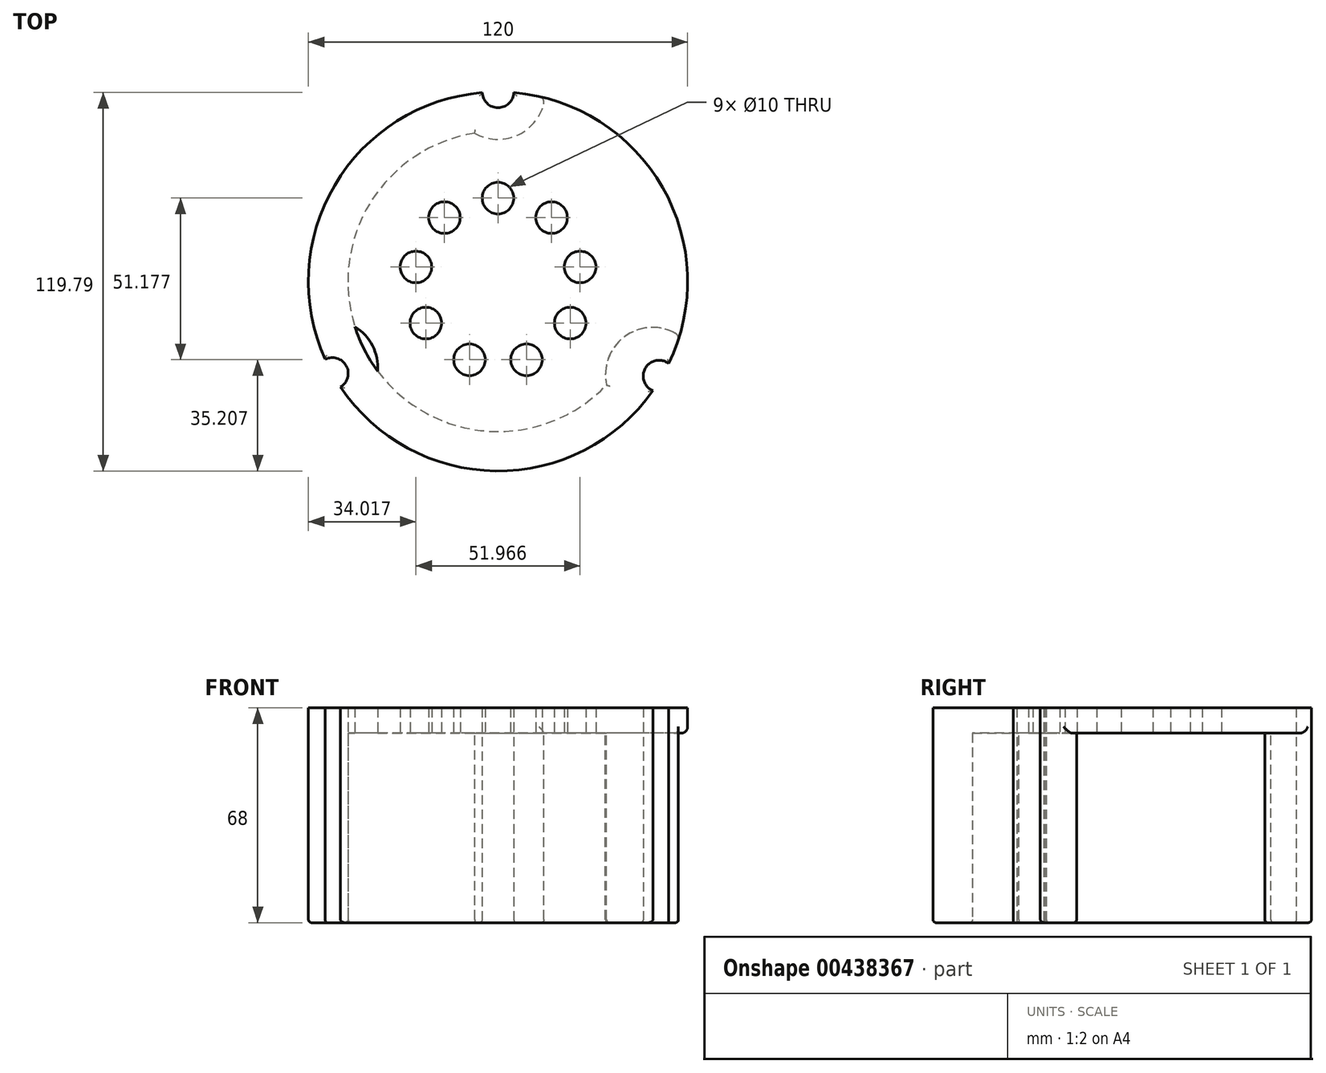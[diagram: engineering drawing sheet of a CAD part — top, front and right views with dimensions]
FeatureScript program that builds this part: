
annotation { "Feature Type Name" : "Feature", "Feature Type Description" : "" }
export const myFeature = defineFeature(function(context is Context, id is Id, definition is map)
    precondition{}
    {
        {
            var Q0;
            Q0=qCreatedBy(makeId("Top.planeOp"),FACE);
            var sketch = newSketch(context, id + "F0", { "sketchPlane" : qUnion([Q0])});
            skCircle(sketch, "E0", {"center": v(0, 0) * mm, "radius": 60 * mm});
            skArc(sketch, "E1", {"start": v(-14.88, 58.12) * mm, "mid": v(0, 45) * mm, "end": v(14.88, 58.12) * mm});
            skArc(sketch, "E2.1.0", {"start": v(-44.9, -39.8) * mm, "mid": v(-39.7, -20.36) * mm, "end": v(-58.52, -13.24) * mm});
            skArc(sketch, "E2.2.0", {"start": v(57.49, -17.18) * mm, "mid": v(36.15, -21.8) * mm, "end": v(42.02, -42.83) * mm});
            skPoint(sketch, "E2.center", {"position": v(-1.35, 1.08) * mm});
            skCircle(sketch, "E3", {"center": v(0, 0) * mm, "radius": 47.5 * mm});
            skArc(sketch, "E4", {"start": v(-5, 59.8) * mm, "mid": v(0, 55) * mm, "end": v(5, 59.8) * mm});
            skArc(sketch, "E5.1.0", {"start": v(-49.85, -33.4) * mm, "mid": v(-48.05, -26.68) * mm, "end": v(-54.7, -24.66) * mm});
            skArc(sketch, "E5.2.0", {"start": v(54.06, -26.03) * mm, "mid": v(46.65, -27.42) * mm, "end": v(49.04, -34.57) * mm});
            skPoint(sketch, "E5.center", {"position": v(-0.48, 0.31) * mm});
            skCircle(sketch, "E6", {"center": v(0, 26.38) * mm, "radius": 5 * mm});
            skCircle(sketch, "E7.1.0", {"center": v(-16.96, 20.21) * mm, "radius": 5 * mm});
            skCircle(sketch, "E7.2.0", {"center": v(-25.98, 4.58) * mm, "radius": 5 * mm});
            skCircle(sketch, "E7.3.0", {"center": v(-22.85, -13.2) * mm, "radius": 5 * mm});
            skCircle(sketch, "E7.4.0", {"center": v(-9.02, -24.8) * mm, "radius": 5 * mm});
            skCircle(sketch, "E7.5.0", {"center": v(9.02, -24.8) * mm, "radius": 5 * mm});
            skCircle(sketch, "E7.6.0", {"center": v(22.85, -13.2) * mm, "radius": 5 * mm});
            skCircle(sketch, "E7.7.0", {"center": v(25.98, 4.58) * mm, "radius": 5 * mm});
            skCircle(sketch, "E7.8.0", {"center": v(16.96, 20.21) * mm, "radius": 5 * mm});
            skSolve(sketch);
        }
        {
            var Q0;
            {var subQ0=sQuery(id+"F0.wireOp",EDGE,"E3");var subQ1=sQuery(id+"F0.wireOp",EDGE,"E1");var subQ2=makeQuery(id+"F0.imprint","INTERSECT",VERTEX,{"disambiguationData":[OD(0.0)],"derivedFrom":[subQ1,subQ0]});Q0=makeQuery(id+"F0.imprint","IMPRINT",FACE,{"disambiguationData":[TD([[makeQuery(id+"F0.imprint","IMPRINT",EDGE,{"disambiguationData":[TD([[subQ2,-1.0]])],"derivedFrom":subQ1}),-1.0]])]});}
            var Q1;
            {var subQ0=sQuery(id+"F0.wireOp",EDGE,"E3");var subQ1=sQuery(id+"F0.wireOp",EDGE,"E2.1.0");var subQ2=makeQuery(id+"F0.imprint","INTERSECT",VERTEX,{"disambiguationData":[OD(0.0)],"derivedFrom":[subQ1,subQ0]});Q1=makeQuery(id+"F0.imprint","IMPRINT",FACE,{"disambiguationData":[TD([[makeQuery(id+"F0.imprint","IMPRINT",EDGE,{"disambiguationData":[TD([[subQ2,-1.0]])],"derivedFrom":subQ1}),1.0]])]});}
            var Q2;
            {var subQ0=sQuery(id+"F0.wireOp",EDGE,"E2.1.0");var subQ1=sQuery(id+"F0.wireOp",EDGE,"E0");var subQ2=makeQuery(id+"F0.imprint","INTERSECT",VERTEX,{"disambiguationData":[OD(0.0)],"derivedFrom":[subQ1,subQ0]});Q2=makeQuery(id+"F0.imprint","IMPRINT",FACE,{"disambiguationData":[TD([[makeQuery(id+"F0.imprint","IMPRINT",EDGE,{"disambiguationData":[TD([[subQ2,1.0]])],"derivedFrom":subQ1}),1.0]])]});}
            var Q3;
            {var subQ0=sQuery(id+"F0.wireOp",EDGE,"E2.1.0");var subQ1=sQuery(id+"F0.wireOp",EDGE,"E0");var subQ2=makeQuery(id+"F0.imprint","INTERSECT",VERTEX,{"disambiguationData":[OD(0.0)],"derivedFrom":[subQ1,subQ0]});Q3=makeQuery(id+"F0.imprint","IMPRINT",FACE,{"disambiguationData":[TD([[makeQuery(id+"F0.imprint","IMPRINT",EDGE,{"disambiguationData":[TD([[subQ2,-1.0]])],"derivedFrom":subQ1}),1.0]])]});}
            var Q4;
            {var subQ0=sQuery(id+"F0.wireOp",EDGE,"E2.2.0");var subQ1=sQuery(id+"F0.wireOp",EDGE,"E0");var subQ2=makeQuery(id+"F0.imprint","INTERSECT",VERTEX,{"disambiguationData":[OD(0.0)],"derivedFrom":[subQ1,subQ0]});Q4=makeQuery(id+"F0.imprint","IMPRINT",FACE,{"disambiguationData":[TD([[makeQuery(id+"F0.imprint","IMPRINT",EDGE,{"disambiguationData":[TD([[subQ2,1.0]])],"derivedFrom":subQ1}),1.0]])]});}
            var Q5;
            {var subQ0=sQuery(id+"F0.wireOp",EDGE,"E3");var subQ1=sQuery(id+"F0.wireOp",EDGE,"E2.2.0");var subQ2=makeQuery(id+"F0.imprint","INTERSECT",VERTEX,{"disambiguationData":[OD(0.0)],"derivedFrom":[subQ1,subQ0]});Q5=makeQuery(id+"F0.imprint","IMPRINT",FACE,{"disambiguationData":[TD([[makeQuery(id+"F0.imprint","IMPRINT",EDGE,{"disambiguationData":[TD([[subQ2,-1.0]])],"derivedFrom":subQ1}),1.0]])]});}
            var Q6;
            {var subQ0=sQuery(id+"F0.wireOp",EDGE,"E1");var subQ1=sQuery(id+"F0.wireOp",EDGE,"E0");var subQ2=makeQuery(id+"F0.imprint","INTERSECT",VERTEX,{"disambiguationData":[OD(1.0)],"derivedFrom":[subQ1,subQ0]});Q6=makeQuery(id+"F0.imprint","IMPRINT",FACE,{"disambiguationData":[TD([[makeQuery(id+"F0.imprint","IMPRINT",EDGE,{"disambiguationData":[TD([[subQ2,1.0]])],"derivedFrom":subQ1}),1.0]])]});}
            var Q7;
            {var subQ0=sQuery(id+"F0.wireOp",EDGE,"E1");var subQ1=sQuery(id+"F0.wireOp",EDGE,"E0");var subQ2=makeQuery(id+"F0.imprint","INTERSECT",VERTEX,{"disambiguationData":[OD(0.0)],"derivedFrom":[subQ1,subQ0]});Q7=makeQuery(id+"F0.imprint","IMPRINT",FACE,{"disambiguationData":[TD([[makeQuery(id+"F0.imprint","IMPRINT",EDGE,{"disambiguationData":[TD([[subQ2,1.0]])],"derivedFrom":subQ1}),1.0]])]});}
            var Q8;
            {var subQ0=sQuery(id+"F0.wireOp",EDGE,"E3");var subQ1=sQuery(id+"F0.wireOp",EDGE,"E1");var subQ2=makeQuery(id+"F0.imprint","INTERSECT",VERTEX,{"disambiguationData":[OD(0.0)],"derivedFrom":[subQ1,subQ0]});Q8=makeQuery(id+"F0.imprint","IMPRINT",FACE,{"disambiguationData":[TD([[makeQuery(id+"F0.imprint","IMPRINT",EDGE,{"disambiguationData":[TD([[subQ2,-1.0]])],"derivedFrom":subQ1}),1.0]])]});}
            var Q9;
            {var subQ0=sQuery(id+"F0.wireOp",EDGE,"E1");var subQ1=sQuery(id+"F0.wireOp",EDGE,"E0");var subQ2=makeQuery(id+"F0.imprint","INTERSECT",VERTEX,{"disambiguationData":[OD(0.0)],"derivedFrom":[subQ1,subQ0]});Q9=makeQuery(id+"F0.imprint","IMPRINT",FACE,{"disambiguationData":[TD([[makeQuery(id+"F0.imprint","IMPRINT",EDGE,{"disambiguationData":[TD([[subQ2,-1.0]])],"derivedFrom":subQ1}),1.0]])]});}
            var Q10;
            {var subQ0=sQuery(id+"F0.wireOp",EDGE,"E1");var subQ1=sQuery(id+"F0.wireOp",EDGE,"E0");var subQ2=makeQuery(id+"F0.imprint","INTERSECT",VERTEX,{"disambiguationData":[OD(1.0)],"derivedFrom":[subQ1,subQ0]});Q10=makeQuery(id+"F0.imprint","IMPRINT",FACE,{"disambiguationData":[TD([[makeQuery(id+"F0.imprint","IMPRINT",EDGE,{"disambiguationData":[TD([[subQ2,-1.0]])],"derivedFrom":subQ1}),1.0]])]});}
            var Q11;
            {var subQ0=sQuery(id+"F0.wireOp",EDGE,"E2.2.0");var subQ1=sQuery(id+"F0.wireOp",EDGE,"E0");var subQ2=makeQuery(id+"F0.imprint","INTERSECT",VERTEX,{"disambiguationData":[OD(1.0)],"derivedFrom":[subQ1,subQ0]});Q11=makeQuery(id+"F0.imprint","IMPRINT",FACE,{"disambiguationData":[TD([[makeQuery(id+"F0.imprint","IMPRINT",EDGE,{"disambiguationData":[TD([[subQ2,-1.0]])],"derivedFrom":subQ1}),1.0]])]});}
            var Q12;
            {var subQ0=sQuery(id+"F0.wireOp",EDGE,"E2.1.0");var subQ1=sQuery(id+"F0.wireOp",EDGE,"E0");var subQ2=makeQuery(id+"F0.imprint","INTERSECT",VERTEX,{"disambiguationData":[OD(1.0)],"derivedFrom":[subQ1,subQ0]});Q12=makeQuery(id+"F0.imprint","IMPRINT",FACE,{"disambiguationData":[TD([[makeQuery(id+"F0.imprint","IMPRINT",EDGE,{"disambiguationData":[TD([[subQ2,-1.0]])],"derivedFrom":subQ1}),1.0]])]});}
            extrude(context, id + "F1", {"entities" : qUnion([Q0, Q1, Q2, Q3, Q4, Q5, Q6, Q7, Q8, Q9, Q10, Q11, Q12]), "depth" : 8 * mm});
        }
        {
            var Q0;
            {var subQ0=sQuery(id+"F0.wireOp",EDGE,"E3");var subQ1=sQuery(id+"F0.wireOp",EDGE,"E1");var subQ2=makeQuery(id+"F0.imprint","INTERSECT",VERTEX,{"disambiguationData":[OD(0.0)],"derivedFrom":[subQ1,subQ0]});Q0=makeQuery(id+"F0.imprint","IMPRINT",FACE,{"disambiguationData":[TD([[makeQuery(id+"F0.imprint","IMPRINT",EDGE,{"disambiguationData":[TD([[subQ2,-1.0]])],"derivedFrom":subQ1}),1.0]])]});}
            var Q1;
            {var subQ0=sQuery(id+"F0.wireOp",EDGE,"E3");var subQ1=sQuery(id+"F0.wireOp",EDGE,"E2.2.0");var subQ2=makeQuery(id+"F0.imprint","INTERSECT",VERTEX,{"disambiguationData":[OD(0.0)],"derivedFrom":[subQ1,subQ0]});Q1=makeQuery(id+"F0.imprint","IMPRINT",FACE,{"disambiguationData":[TD([[makeQuery(id+"F0.imprint","IMPRINT",EDGE,{"disambiguationData":[TD([[subQ2,-1.0]])],"derivedFrom":subQ1}),1.0]])]});}
            var Q2;
            {var subQ0=sQuery(id+"F0.wireOp",EDGE,"E3");var subQ1=sQuery(id+"F0.wireOp",EDGE,"E2.1.0");var subQ2=makeQuery(id+"F0.imprint","INTERSECT",VERTEX,{"disambiguationData":[OD(0.0)],"derivedFrom":[subQ1,subQ0]});Q2=makeQuery(id+"F0.imprint","IMPRINT",FACE,{"disambiguationData":[TD([[makeQuery(id+"F0.imprint","IMPRINT",EDGE,{"disambiguationData":[TD([[subQ2,-1.0]])],"derivedFrom":subQ1}),1.0]])]});}
            var Q3;
            {var subQ0=sQuery(id+"F0.wireOp",EDGE,"E2.1.0");var subQ1=sQuery(id+"F0.wireOp",EDGE,"E0");var subQ2=makeQuery(id+"F0.imprint","INTERSECT",VERTEX,{"disambiguationData":[OD(0.0)],"derivedFrom":[subQ1,subQ0]});Q3=makeQuery(id+"F0.imprint","IMPRINT",FACE,{"disambiguationData":[TD([[makeQuery(id+"F0.imprint","IMPRINT",EDGE,{"disambiguationData":[TD([[subQ2,1.0]])],"derivedFrom":subQ1}),1.0]])]});}
            var Q4;
            {var subQ0=sQuery(id+"F0.wireOp",EDGE,"E2.2.0");var subQ1=sQuery(id+"F0.wireOp",EDGE,"E0");var subQ2=makeQuery(id+"F0.imprint","INTERSECT",VERTEX,{"disambiguationData":[OD(0.0)],"derivedFrom":[subQ1,subQ0]});Q4=makeQuery(id+"F0.imprint","IMPRINT",FACE,{"disambiguationData":[TD([[makeQuery(id+"F0.imprint","IMPRINT",EDGE,{"disambiguationData":[TD([[subQ2,1.0]])],"derivedFrom":subQ1}),1.0]])]});}
            var Q5;
            {var subQ0=sQuery(id+"F0.wireOp",EDGE,"E1");var subQ1=sQuery(id+"F0.wireOp",EDGE,"E0");var subQ2=makeQuery(id+"F0.imprint","INTERSECT",VERTEX,{"disambiguationData":[OD(0.0)],"derivedFrom":[subQ1,subQ0]});Q5=makeQuery(id+"F0.imprint","IMPRINT",FACE,{"disambiguationData":[TD([[makeQuery(id+"F0.imprint","IMPRINT",EDGE,{"disambiguationData":[TD([[subQ2,1.0]])],"derivedFrom":subQ1}),1.0]])]});}
            var Q6;
            {var subQ0=sQuery(id+"F0.wireOp",EDGE,"E2.1.0");var subQ1=sQuery(id+"F0.wireOp",EDGE,"E0");var subQ2=makeQuery(id+"F0.imprint","INTERSECT",VERTEX,{"disambiguationData":[OD(1.0)],"derivedFrom":[subQ1,subQ0]});Q6=makeQuery(id+"F0.imprint","IMPRINT",FACE,{"disambiguationData":[TD([[makeQuery(id+"F0.imprint","IMPRINT",EDGE,{"disambiguationData":[TD([[subQ2,-1.0]])],"derivedFrom":subQ1}),1.0]])]});}
            var Q7;
            {var subQ0=sQuery(id+"F0.wireOp",EDGE,"E1");var subQ1=sQuery(id+"F0.wireOp",EDGE,"E0");var subQ2=makeQuery(id+"F0.imprint","INTERSECT",VERTEX,{"disambiguationData":[OD(1.0)],"derivedFrom":[subQ1,subQ0]});Q7=makeQuery(id+"F0.imprint","IMPRINT",FACE,{"disambiguationData":[TD([[makeQuery(id+"F0.imprint","IMPRINT",EDGE,{"disambiguationData":[TD([[subQ2,-1.0]])],"derivedFrom":subQ1}),1.0]])]});}
            var Q8;
            {var subQ0=sQuery(id+"F0.wireOp",EDGE,"E2.2.0");var subQ1=sQuery(id+"F0.wireOp",EDGE,"E0");var subQ2=makeQuery(id+"F0.imprint","INTERSECT",VERTEX,{"disambiguationData":[OD(1.0)],"derivedFrom":[subQ1,subQ0]});Q8=makeQuery(id+"F0.imprint","IMPRINT",FACE,{"disambiguationData":[TD([[makeQuery(id+"F0.imprint","IMPRINT",EDGE,{"disambiguationData":[TD([[subQ2,-1.0]])],"derivedFrom":subQ1}),1.0]])]});}
            extrude(context, id + "F2", {"entities" : qUnion([Q0, Q1, Q2, Q3, Q4, Q5, Q6, Q7, Q8]), "operationType" : NewBodyOperationType.ADD, "oppositeDirection" : true, "depth" : 60 * mm});
        }
        {
            var Q0;
            {var subQ0=sQuery(id+"F0.wireOp",EDGE,"E0");var subQ1=makeQuery(id+"F0.imprint","INTERSECT",VERTEX,{"disambiguationData":[OD(1.0)],"derivedFrom":[subQ0,sQuery(id+"F0.wireOp",EDGE,"E2.2.0")]});var subQ2=makeQuery(id+"F0.imprint","INTERSECT",VERTEX,{"disambiguationData":[OD(0.0)],"derivedFrom":[subQ0,sQuery(id+"F0.wireOp",EDGE,"E2.1.0")]});Q0=makeQuery(id+"F1.opExtrude","CAP_EDGE",EDGE,{"disambiguationData":[OSD([subQ0]),TDD([makeQuery(id+"F0.imprint","IMPRINT",EDGE,{"disambiguationData":[TD([[subQ2,1.0]])],"derivedFrom":subQ0}),makeQuery(id+"F0.imprint","IMPRINT",EDGE,{"disambiguationData":[TD([[subQ2,-1.0]])],"derivedFrom":subQ0}),makeQuery(id+"F0.imprint","IMPRINT",EDGE,{"disambiguationData":[TD([[subQ1,-1.0]])],"derivedFrom":subQ0})])],"isStart":true});}
            var Q1;
            {var subQ0=sQuery(id+"F0.wireOp",EDGE,"E2.1.0");var subQ1=sQuery(id+"F0.wireOp",EDGE,"E0");Q1=makeQuery(id+"F2.opExtrude","SWEPT_EDGE",EDGE,{"disambiguationData":[OSD([subQ1,subQ0]),TDD([makeQuery(id+"F0.imprint","INTERSECT",VERTEX,{"disambiguationData":[OD(0.0)],"derivedFrom":[subQ1,subQ0]})])]});}
            var Q2;
            {var subQ0=sQuery(id+"F0.wireOp",EDGE,"E2.2.0");var subQ1=sQuery(id+"F0.wireOp",EDGE,"E0");Q2=makeQuery(id+"F2.opExtrude","SWEPT_EDGE",EDGE,{"disambiguationData":[OSD([subQ1,subQ0]),TDD([makeQuery(id+"F0.imprint","INTERSECT",VERTEX,{"disambiguationData":[OD(1.0)],"derivedFrom":[subQ1,subQ0]})])]});}
            var Q3;
            {var subQ0=sQuery(id+"F0.wireOp",EDGE,"E0");var subQ1=makeQuery(id+"F0.imprint","INTERSECT",VERTEX,{"disambiguationData":[OD(1.0)],"derivedFrom":[subQ0,sQuery(id+"F0.wireOp",EDGE,"E1")]});var subQ2=makeQuery(id+"F0.imprint","INTERSECT",VERTEX,{"disambiguationData":[OD(0.0)],"derivedFrom":[subQ0,sQuery(id+"F0.wireOp",EDGE,"E2.2.0")]});Q3=makeQuery(id+"F1.opExtrude","CAP_EDGE",EDGE,{"disambiguationData":[OSD([subQ0]),TDD([makeQuery(id+"F0.imprint","IMPRINT",EDGE,{"disambiguationData":[TD([[subQ1,-1.0]])],"derivedFrom":subQ0}),makeQuery(id+"F0.imprint","IMPRINT",EDGE,{"disambiguationData":[TD([[subQ2,1.0]])],"derivedFrom":subQ0}),makeQuery(id+"F0.imprint","IMPRINT",EDGE,{"disambiguationData":[TD([[subQ1,1.0]])],"derivedFrom":subQ0})])],"isStart":true});}
            var Q4;
            {var subQ0=sQuery(id+"F0.wireOp",EDGE,"E2.2.0");var subQ1=sQuery(id+"F0.wireOp",EDGE,"E0");Q4=makeQuery(id+"F2.opExtrude","SWEPT_EDGE",EDGE,{"disambiguationData":[OSD([subQ1,subQ0]),TDD([makeQuery(id+"F0.imprint","INTERSECT",VERTEX,{"disambiguationData":[OD(0.0)],"derivedFrom":[subQ1,subQ0]})])]});}
            var Q5;
            {var subQ0=sQuery(id+"F0.wireOp",EDGE,"E1");var subQ1=sQuery(id+"F0.wireOp",EDGE,"E0");Q5=makeQuery(id+"F2.opExtrude","SWEPT_EDGE",EDGE,{"disambiguationData":[OSD([subQ1,subQ0]),TDD([makeQuery(id+"F0.imprint","INTERSECT",VERTEX,{"disambiguationData":[OD(1.0)],"derivedFrom":[subQ1,subQ0]})])]});}
            var Q6;
            {var subQ0=sQuery(id+"F0.wireOp",EDGE,"E1");var subQ1=sQuery(id+"F0.wireOp",EDGE,"E0");Q6=makeQuery(id+"F2.opExtrude","SWEPT_EDGE",EDGE,{"disambiguationData":[OSD([subQ1,subQ0]),TDD([makeQuery(id+"F0.imprint","INTERSECT",VERTEX,{"disambiguationData":[OD(0.0)],"derivedFrom":[subQ1,subQ0]})])]});}
            var Q7;
            {var subQ0=sQuery(id+"F0.wireOp",EDGE,"E2.1.0");var subQ1=sQuery(id+"F0.wireOp",EDGE,"E0");Q7=makeQuery(id+"F2.opExtrude","SWEPT_EDGE",EDGE,{"disambiguationData":[OSD([subQ1,subQ0]),TDD([makeQuery(id+"F0.imprint","INTERSECT",VERTEX,{"disambiguationData":[OD(1.0)],"derivedFrom":[subQ1,subQ0]})])]});}
            var Q8;
            {var subQ0=sQuery(id+"F0.wireOp",EDGE,"E0");var subQ1=makeQuery(id+"F0.imprint","INTERSECT",VERTEX,{"disambiguationData":[OD(1.0)],"derivedFrom":[subQ0,sQuery(id+"F0.wireOp",EDGE,"E2.1.0")]});var subQ2=makeQuery(id+"F0.imprint","INTERSECT",VERTEX,{"disambiguationData":[OD(0.0)],"derivedFrom":[subQ0,sQuery(id+"F0.wireOp",EDGE,"E1")]});Q8=makeQuery(id+"F1.opExtrude","CAP_EDGE",EDGE,{"disambiguationData":[OSD([subQ0]),TDD([makeQuery(id+"F0.imprint","IMPRINT",EDGE,{"disambiguationData":[TD([[subQ2,1.0]])],"derivedFrom":subQ0}),makeQuery(id+"F0.imprint","IMPRINT",EDGE,{"disambiguationData":[TD([[subQ2,-1.0]])],"derivedFrom":subQ0}),makeQuery(id+"F0.imprint","IMPRINT",EDGE,{"disambiguationData":[TD([[subQ1,-1.0]])],"derivedFrom":subQ0})])],"isStart":true});}
            fillet(context, id + "F3", {"entities" : qUnion([Q0, Q1, Q2, Q3, Q4, Q5, Q6, Q7, Q8]), "radius" : 2 * mm, "tangentPropagation" : true, "allowEdgeOverflow" : false});
        }
        {
            var Q0;
            Q0=makeQuery(id+"F2.opExtrude","CAP_FACE",FACE,{"disambiguationData":[OSD([sQuery(id+"F0.wireOp",EDGE,"E0"),sQuery(id+"F0.wireOp",EDGE,"E2.1.0"),sQuery(id+"F0.wireOp",EDGE,"E3"),sQuery(id+"F0.wireOp",EDGE,"E5.1.0")])],"isStart":false});
            var Q1;
            Q1=makeQuery(id+"F2.opExtrude","CAP_FACE",FACE,{"disambiguationData":[OSD([sQuery(id+"F0.wireOp",EDGE,"E0"),sQuery(id+"F0.wireOp",EDGE,"E1"),sQuery(id+"F0.wireOp",EDGE,"E3"),sQuery(id+"F0.wireOp",EDGE,"E4")])],"isStart":false});
            var Q2;
            Q2=makeQuery(id+"F2.opExtrude","CAP_FACE",FACE,{"disambiguationData":[OSD([sQuery(id+"F0.wireOp",EDGE,"E0"),sQuery(id+"F0.wireOp",EDGE,"E2.2.0"),sQuery(id+"F0.wireOp",EDGE,"E3"),sQuery(id+"F0.wireOp",EDGE,"E5.2.0")])],"isStart":false});
            fillet(context, id + "F4", {"entities" : qUnion([Q0, Q1, Q2]), "radius" : 1 * mm, "tangentPropagation" : true, "allowEdgeOverflow" : false});
        }
    });
